FCSTD DOCUMENT  (FreeCAD 1.0R39285 (Git))
Label: optical-system
License: All rights reserved
objects: Part::Feature×51, App::Link×23, App::FeaturePython×23, App::Part×13, PartDesign::FeatureBase×1, Sketcher::SketchObject×1, PartDesign::Pocket×1, PartDesign::Body×1, Assembly::JointGroup×1, Assembly::AssemblyObject×1
note: 59 computed .brp shape members not serialized (recipe doc carries the construction recipe); baked Part::Feature solids carry a one-line shape summary decoded from their .brp

FEATURE [Part::Feature] Part__Feature  label="TTN210411-E0W"
  shape: bbox 50.8 x 39.62 x 50.8 mm, 414 faces (baked)
FEATURE [Part::Feature] Part__Feature001  label="TTN210411-E0W001"
  shape: bbox 5.001 x 4.001 x 4.001 mm, 29 faces (baked)
FEATURE [Part::Feature] Part__Feature002  label="TTN210411-E0W002"
  shape: bbox 5.001 x 4.001 x 4.001 mm, 29 faces (baked)
FEATURE [Part::Feature] Part__Feature003  label="TTN210411-E0W003"
  shape: bbox 5.001 x 4.001 x 4.001 mm, 29 faces (baked)
FEATURE [Part::Feature] Part__Feature004  label="TTN210411-E0W004"
  shape: bbox 5.001 x 4.001 x 4.001 mm, 29 faces (baked)
FEATURE [Part::Feature] Part__Feature005  label="TTN210411-E0W005"
  shape: bbox 5.001 x 4.001 x 4.001 mm, 29 faces (baked)
FEATURE [Part::Feature] Part__Feature006  label="TTN210411-E0W006"
  shape: bbox 5.001 x 4.001 x 4.001 mm, 29 faces (baked)
FEATURE [Part::Feature] Part__Feature007  label="TTN210411-E0W007"
  shape: bbox 5.001 x 4.001 x 4.001 mm, 29 faces (baked)
FEATURE [Part::Feature] Part__Feature008  label="TTN210411-E0W008"
  shape: bbox 5.001 x 4.001 x 4.001 mm, 29 faces (baked)
FEATURE [App::Part] TTN210411_E0W  label="C6WR"
  Group = -> [Part__Feature,Part__Feature001,Part__Feature002,Part__Feature003,Part__Feature004,Part__Feature005,Part__Feature006,Part__Feature007,Part__Feature008]
  Origin = -> Origin001
FEATURE [App::Link] C6WR  label="C6WR001"
  LinkPlacement = pos=(25.4,-25.4,5.02654e-06) rot=(0.577351,0.57735,-0.57735;2.0944rad)
  LinkedObject = -> TTN210411_E0W
  Placement = pos=(25.4,-25.4,5.02654e-06) rot=(0.577351,0.57735,-0.57735;2.0944rad)
FEATURE [App::FeaturePython] GroundedJoint  # Assembly grounded joint (typed FeaturePython)
  ObjectToGround = -> C6WR
  Placement = pos=(25.4,-25.4,5.02654e-06) rot=(0.577351,0.57735,-0.57735;2.0944rad)
FEATURE [Part::Feature] Part__Feature009  label="20587-E0W"
  shape: bbox 18.51 x 30.48 x 30.48 mm, 108 faces (baked)
FEATURE [Part::Feature] Part__Feature010  label="20587-E0W001"
  shape: bbox 10 x 32.78 x 32.91 mm, 10 faces (baked)
FEATURE [Part::Feature] Part__Feature011  label="20587-E0W002"
  shape: bbox 10.38 x 35.13 x 35.16 mm, 27 faces (baked)
FEATURE [Part::Feature] Part__Feature012  label="20587-E0W003"
  shape: bbox 2.484 x 26.29 x 30.36 mm, 38 faces (baked)
FEATURE [App::Part] _0587_E0W  label="AC254-040-A-ML"
  Group = -> [Part__Feature009,Part__Feature010,Part__Feature011,Part__Feature012]
  Origin = -> Origin002
FEATURE [Part::Feature] Part__Feature013  label="0875-E0W"
  shape: bbox 5.994 x 76.2 x 5.994 mm, 20 faces (baked)
FEATURE [App::Link] ER3_000  label="ER3-001"
  LinkPlacement = pos=(11.466,16.1264,-86.4141) rot=(-1,0,0;1.5708rad)
  LinkedObject = -> _875_E0W
  Placement = pos=(11.466,16.1264,-86.4141) rot=(-1,0,0;1.5708rad)
FEATURE [App::FeaturePython] Joint  label="Fixed"  # Assembly joint (typed FeaturePython)
  Activated = true
  AngleMax = 0
  AngleMin = 0
  Detach1 = false
  Detach2 = false
  Distance = 0
  Distance2 = 0
  EnableAngleMax = false
  EnableAngleMin = false
  EnableLengthMax = false
  EnableLengthMin = false
  JointType = 0 (Fixed)
  LengthMax = 0
  LengthMin = 0
  Placement1 = pos=(-1.06592,-35.6141,-1.12644) rot=(0.57735,0.57735,0.57735;4.18879rad)
  Placement2 = pos=(50.8,-14.9999,-40.4) rot=(-0.707107,0,0.707107;3.14159rad)
  Reference1 = -> Assembly [ER3_000.Part__Feature013.Edge6,ER3_000.Part__Feature013.Edge6]
  Reference2 = -> Assembly [C6WR.Part__Feature.Edge507,C6WR.Part__Feature.Edge507]
FEATURE [App::Link] ER3_001  label="ER3-002"
  LinkPlacement = pos=(41.4659,-13.8736,-86.414) rot=(-1,0,0;1.5708rad)
  LinkedObject = -> _875_E0W
  Placement = pos=(41.4659,-13.8736,-86.414) rot=(-1,0,0;1.5708rad)
FEATURE [App::Link] ER3_002  label="ER3-003"
  LinkPlacement = pos=(9.33417,-16.1264,-86.4141) rot=(0,0.707107,-0.707107;3.14159rad)
  LinkedObject = -> _875_E0W
  Placement = pos=(9.33417,-16.1264,-86.4141) rot=(0,0.707107,-0.707107;3.14159rad)
FEATURE [App::Link] ER3_003  label="ER3-004"
  LinkPlacement = pos=(39.3341,13.8736,-86.414) rot=(0,0.707107,-0.707107;3.14159rad)
  LinkedObject = -> _875_E0W
  Placement = pos=(39.3341,13.8736,-86.414) rot=(0,0.707107,-0.707107;3.14159rad)
FEATURE [App::FeaturePython] Joint001  label="Fixed001"  # Assembly joint (typed FeaturePython)
  Activated = true
  AngleMax = 0
  AngleMin = 0
  Detach1 = false
  Detach2 = false
  Distance = 0
  Distance2 = 0
  EnableAngleMax = false
  EnableAngleMin = false
  EnableLengthMax = false
  EnableLengthMin = false
  JointType = 0 (Fixed)
  LengthMax = 0
  LengthMin = 0
  Placement1 = pos=(-1.06592,-35.6141,-1.12644) rot=(0.57735,0.57735,0.57735;4.18879rad)
  Placement2 = pos=(50.8,14.9999,-40.4) rot=(0,-1,0;1.5708rad)
  Reference1 = -> Assembly [ER3_003.Part__Feature013.Edge6,ER3_003.Part__Feature013.Edge6]
  Reference2 = -> Assembly [C6WR.Part__Feature.Edge505,C6WR.Part__Feature.Edge505]
FEATURE [App::FeaturePython] Joint002  label="Fixed002"  # Assembly joint (typed FeaturePython)
  Activated = true
  AngleMax = 0
  AngleMin = 0
  Detach1 = false
  Detach2 = false
  Distance = 0
  Distance2 = 0
  EnableAngleMax = false
  EnableAngleMin = false
  EnableLengthMax = false
  EnableLengthMin = false
  JointType = 0 (Fixed)
  LengthMax = 0
  LengthMin = 0
  Placement1 = pos=(-1.06592,-35.6141,-1.12644) rot=(0.57735,0.57735,0.57735;4.18879rad)
  Placement2 = pos=(50.8,-14.9999,-10.4) rot=(0,-1,0;1.5708rad)
  Reference1 = -> Assembly [ER3_002.Part__Feature013.Edge6,ER3_002.Part__Feature013.Edge6]
  Reference2 = -> Assembly [C6WR.Part__Feature.Edge506,C6WR.Part__Feature.Edge506]
FEATURE [App::FeaturePython] Joint003  label="Fixed003"  # Assembly joint (typed FeaturePython)
  Activated = true
  AngleMax = 0
  AngleMin = 0
  Detach1 = false
  Detach2 = false
  Distance = 0
  Distance2 = 0
  EnableAngleMax = false
  EnableAngleMin = false
  EnableLengthMax = false
  EnableLengthMin = false
  JointType = 0 (Fixed)
  LengthMax = 0
  LengthMin = 0
  Placement1 = pos=(-1.06592,-35.6141,-1.12644) rot=(0.57735,0.57735,0.57735;4.18879rad)
  Placement2 = pos=(50.8,14.9999,-10.4) rot=(-0.707107,0,0.707107;3.14159rad)
  Reference1 = -> Assembly [ER3_001.Part__Feature013.Edge6,ER3_001.Part__Feature013.Edge6]
  Reference2 = -> Assembly [C6WR.Part__Feature.Edge504,C6WR.Part__Feature.Edge504]
FEATURE [Part::Feature] Part__Feature015  label="0875-E0W002"
  shape: bbox 3.285 x 6.668 x 2.845 mm, 51 faces (baked)
FEATURE [App::Part] _875_E0W  label="ER3-000"
  Group = -> [Part__Feature013,Part__Feature015]
  Origin = -> Origin003
FEATURE [Part::Feature] Part__Feature016  label="TTN189114-E0W"
  shape: bbox 40.64 x 40.64 x 8.89 mm, 368 faces (baked)
FEATURE [Part::Feature] Part__Feature017  label="TTN189114-E0W001"
  shape: bbox 5.001 x 4.001 x 4.001 mm, 29 faces (baked)
FEATURE [Part::Feature] Part__Feature018  label="TTN189114-E0W002"
  shape: bbox 5.001 x 4.001 x 4.001 mm, 29 faces (baked)
FEATURE [Part::Feature] Part__Feature019  label="TTN189114-E0W003"
  shape: bbox 5.001 x 4.001 x 4.001 mm, 29 faces (baked)
FEATURE [Part::Feature] Part__Feature020  label="TTN189114-E0W004"
  shape: bbox 5.001 x 4.001 x 4.001 mm, 29 faces (baked)
FEATURE [App::Part] TTN189114_E0W  label="CP33-000"
  Group = -> [Part__Feature016,Part__Feature017,Part__Feature018,Part__Feature019,Part__Feature020]
  Origin = -> Origin004
FEATURE [App::Link] CP33_000  label="CP33-001"
  LinkPlacement = pos=(25.4001,-2.5535e-05,-66.047) rot=(-0.707107,0.707107,0;3.14159rad)
  LinkedObject = -> TTN189114_E0W
  Placement = pos=(25.4001,-2.5535e-05,-66.047) rot=(-0.707107,0.707107,0;3.14159rad)
FEATURE [App::FeaturePython] Joint004  label="Fixed004"  # Assembly joint (typed FeaturePython)
  Activated = true
  AngleMax = 0
  AngleMin = 0
  Detach1 = false
  Detach2 = false
  Distance = 0
  Distance2 = 0
  EnableAngleMax = false
  EnableAngleMin = false
  EnableLengthMax = false
  EnableLengthMin = false
  JointType = 0 (Fixed)
  LengthMax = 0
  LengthMin = 0
  Offset2 = pos=(0,0,-56) rot=(0,0,1;0rad)
  Placement1 = pos=(15,15,4.191) rot=(0,0,1;0rad)
  Placement2 = pos=(-1.06592,-16.1761,-1.12644) rot=(0.57735,0.57735,0.57735;4.18879rad)
  Reference1 = -> Assembly [CP33_000.Part__Feature016.Edge399,CP33_000.Part__Feature016.Edge399]
  Reference2 = -> Assembly [ER3_002.Part__Feature013.Edge26,ER3_002.Part__Feature013.Edge26]
FEATURE [App::Link] AC254_040_A_ML  label="AC254-040-A-ML001"
  LinkPlacement = pos=(26.1111,6.72322,-89.4656) rot=(0.577351,0.57735,-0.57735;2.0944rad)
  LinkedObject = -> _0587_E0W
  Placement = pos=(26.1111,6.72322,-89.4656) rot=(0.577351,0.57735,-0.57735;2.0944rad)
FEATURE [App::FeaturePython] Joint005  label="Fixed005"  # Assembly joint (typed FeaturePython)
  Activated = true
  AngleMax = 0
  AngleMin = 0
  Detach1 = false
  Detach2 = false
  Distance = 0
  Distance2 = 0
  EnableAngleMax = false
  EnableAngleMin = false
  EnableLengthMax = false
  EnableLengthMin = false
  JointType = 0 (Fixed)
  LengthMax = 0
  LengthMin = 0
  Placement1 = pos=(-19.4136,-0.711014,6.72325) rot=(0,-1,0;1.5708rad)
  Placement2 = pos=(-4.16e-14,-3.12e-14,4.00506) rot=(0,0,1;0rad)
  Reference1 = -> Assembly [AC254_040_A_ML.Part__Feature009.Edge7,AC254_040_A_ML.Part__Feature009.Edge7]
  Reference2 = -> Assembly [CP33_000.Part__Feature016.Edge77,CP33_000.Part__Feature016.Edge77]
FEATURE [Part::Feature] Part__Feature021  label="TTN189038-E0W"
  shape: bbox 40.64 x 40.64 x 8.89 mm, 607 faces (baked)
FEATURE [Part::Feature] Part__Feature022  label="TTN189038-E0W001"
  shape: bbox 5.001 x 4.001 x 4.001 mm, 29 faces (baked)
FEATURE [Part::Feature] Part__Feature023  label="TTN189038-E0W002"
  shape: bbox 5.001 x 4.001 x 4.001 mm, 29 faces (baked)
FEATURE [Part::Feature] Part__Feature024  label="TTN189038-E0W003"
  shape: bbox 5.001 x 4.001 x 4.001 mm, 29 faces (baked)
FEATURE [Part::Feature] Part__Feature025  label="TTN189038-E0W004"
  shape: bbox 5.001 x 4.001 x 4.001 mm, 29 faces (baked)
FEATURE [App::Part] TTN189038_E0W  label="CP42-000"
  Group = -> [Part__Feature021,Part__Feature022,Part__Feature023,Part__Feature024,Part__Feature025]
  Origin = -> Origin005
FEATURE [App::Link] CP42_000  label="CP42-001"
  LinkPlacement = pos=(7.29353,-2.18583,-119.261) rot=(1,0,0;3.14159rad)
  LinkedObject = -> TTN189038_E0W
  Placement = pos=(7.29353,-2.18583,-119.261) rot=(1,0,0;3.14159rad)
FEATURE [App::FeaturePython] Joint006  label="Fixed006"  # Assembly joint (typed FeaturePython)
  Activated = true
  AngleMax = 0
  AngleMin = 0
  Detach1 = false
  Detach2 = false
  Distance = 0
  Distance2 = 0
  EnableAngleMax = false
  EnableAngleMin = false
  EnableLengthMax = false
  EnableLengthMin = false
  JointType = 0 (Fixed)
  LengthMax = 0
  LengthMin = 0
  Offset2 = pos=(0,0,-20) rot=(0,0,-1;1.5708rad)
  Placement1 = pos=(3.10658,12.8142,-12.2606) rot=(1,0,0;3.14159rad)
  Placement2 = pos=(-1.06592,20.5859,-1.12644) rot=(0,0.707107,0.707107;3.14159rad)
  Reference1 = -> Assembly [CP42_000.Part__Feature021.Edge53,CP42_000.Part__Feature021.Edge53]
  Reference2 = -> Assembly [ER3_002.Part__Feature013.Edge28,ER3_002.Part__Feature013.Edge28]
FEATURE [Part::Feature] Part__Feature026  label="TTN088605-E0W"
  shape: bbox 38.79 x 26.13 x 26.13 mm, 502 faces, 0 solids (baked)
FEATURE [Part::Feature] Part__Feature027  label="TTN088605-E0W001"
  shape: bbox 0.3121 x 0.2897 x 0.041 mm, 1 faces, 0 solids (baked)
FEATURE [App::Part] TTN088605_E0W  label="RMS10X"
  Group = -> [Part__Feature026,Part__Feature027]
  Origin = -> Origin006
FEATURE [App::Link] RMS10X  label="RMS10X001"
  LinkPlacement = pos=(43.629,23.975,-127.528) rot=(0,1,0;4.71239rad)
  LinkedObject = -> TTN088605_E0W
  Placement = pos=(43.629,23.975,-127.528) rot=(0,1,0;4.71239rad)
FEATURE [App::FeaturePython] Joint007  label="Fixed007"  # Assembly joint (typed FeaturePython)
  Activated = true
  AngleMax = 0
  AngleMin = 0
  Detach1 = false
  Detach2 = false
  Distance = 0
  Distance2 = 0
  EnableAngleMax = false
  EnableAngleMin = false
  EnableLengthMax = false
  EnableLengthMin = false
  JointType = 0 (Fixed)
  LengthMax = 0
  LengthMin = 0
  Offset2 = pos=(0,0,-2.5) rot=(0,0,1;0rad)
  Placement1 = pos=(14.8319,-23.975,18.2289) rot=(0,1,0;1.5708rad)
  Placement2 = pos=(18.1066,-2.18581,-6.56454) rot=(0,0,1;0rad)
  Reference1 = -> Assembly [RMS10X.Part__Feature026.Edge375,RMS10X.Part__Feature026.Edge375]
  Reference2 = -> Assembly [CP42_000.Part__Feature021.Edge25,CP42_000.Part__Feature021.Edge25]
FEATURE [Part::Feature] Part__Feature028  label="24004-E0W"
  shape: bbox 50.29 x 9.398 x 50.29 mm, 65 faces (baked)
FEATURE [Part::Feature] Part__Feature029  label="24004-E0W001"
  shape: bbox 42.67 x 12.07 x 42.67 mm, 217 faces (baked)
FEATURE [Part::Feature] Part__Feature030  label="24004-E0W002"
  shape: bbox 47.75 x 5.842 x 47.75 mm, 1692 faces (baked)
FEATURE [Part::Feature] Part__Feature031  label="24004-E0W003"
  shape: bbox 4.215 x 3.799 x 4.215 mm, 58 faces (baked)
FEATURE [App::Part] _4004_E0W  label="B3CR-000"
  Group = -> [Part__Feature028,Part__Feature029,Part__Feature030,Part__Feature031]
  Origin = -> Origin007
FEATURE [App::Link] B3CR_000  label="B3CR-001"
  LinkPlacement = pos=(48.514,-2.06884e-06,-25.4) rot=(-0.485653,0.485653,0.726831;1.88458rad)
  LinkedObject = -> _4004_E0W
  Placement = pos=(48.514,-2.06884e-06,-25.4) rot=(-0.485653,0.485653,0.726831;1.88458rad)
FEATURE [Part::Feature] Part__Feature032  label="TTN005913-E0W"
  shape: bbox 49.78 x 1.905 x 49.78 mm, 56 faces (baked)
FEATURE [Part::Feature] Part__Feature033  label="TTN005913-E0W001"
  Placement = pos=(0,0,0) rot=(0,1,0;3.92699rad)
  shape: bbox 41.91 x 8.763 x 41.91 mm, 301 faces (baked)
FEATURE [App::Part] TTN005913_E0W  label="C6WA-000"
  Group = -> [Part__Feature032,Part__Feature033]
  Origin = -> Origin008
FEATURE [App::Link] C6WA_000  label="C6WA-001"
  LinkPlacement = pos=(47.117,-1.92568e-06,-25.4) rot=(0,0,1;1.5708rad)
  LinkedObject = -> TTN005913_E0W
  Placement = pos=(47.117,-1.92568e-06,-25.4) rot=(0,0,1;1.5708rad)
FEATURE [App::FeaturePython] Joint008  label="Fixed008"  # Assembly joint (typed FeaturePython)
  Activated = true
  AngleMax = 0
  AngleMin = 0
  Detach1 = false
  Detach2 = false
  Distance = 0
  Distance2 = 0
  EnableAngleMax = false
  EnableAngleMin = false
  EnableLengthMax = false
  EnableLengthMin = false
  JointType = 0 (Fixed)
  LengthMax = 0
  LengthMin = 0
  Offset2 = pos=(0,0,0) rot=(0,0,-1;1.5708rad)
  Placement1 = pos=(19.05,1.905,19.05) rot=(0.57735,-0.57735,0.57735;2.0944rad)
  Placement2 = pos=(6.35,19.812,-44.45) rot=(0,0.707107,0.707107;3.14159rad)
  Reference1 = -> Assembly [C6WA_000.Part__Feature032.Edge63,C6WA_000.Part__Feature032.Edge63]
  Reference2 = -> Assembly [C6WR.Part__Feature.Edge523,C6WR.Part__Feature.Edge523]
FEATURE [App::FeaturePython] Joint009  label="Fixed009"  # Assembly joint (typed FeaturePython)
  Activated = true
  AngleMax = 0
  AngleMin = 0
  Detach1 = false
  Detach2 = false
  Distance = 0
  Distance2 = 0
  EnableAngleMax = false
  EnableAngleMin = false
  EnableLengthMax = false
  EnableLengthMin = false
  JointType = 0 (Fixed)
  LengthMax = 0
  LengthMin = 0
  Offset2 = pos=(0,0,0) rot=(0,0,1;0.392699rad)
  Placement1 = pos=(-1.5e-15,4.699,1.9e-15) rot=(-0.281085,0.678598,-0.678598;3.68962rad)
  Placement2 = pos=(0,3.302,0) rot=(-0.427192,-0.639338,-0.639338;2.33414rad)
  Reference1 = -> Assembly [B3CR_000.Part__Feature029.Edge36,B3CR_000.Part__Feature029.Edge36]
  Reference2 = -> Assembly [C6WA_000.Part__Feature033.Edge299,C6WA_000.Part__Feature033.Edge299]
FEATURE [Part::Feature] Part__Feature034  label="1674-E0W"
  shape: bbox 5.994 x 203.2 x 5.994 mm, 20 faces (baked)
FEATURE [Part::Feature] Part__Feature035  label="1674-E0W001"
  shape: bbox 2.927 x 6.668 x 3.281 mm, 51 faces (baked)
FEATURE [Part::Feature] Part__Feature036  label="1674-E0W002"
  shape: bbox 3.285 x 6.668 x 2.845 mm, 51 faces (baked)
FEATURE [App::Part] _674_E0W  label="ER8-000"
  Group = -> [Part__Feature034,Part__Feature035,Part__Feature036]
  Origin = -> Origin009
FEATURE [App::Link] ER8_000  label="ER8-001"
  LinkPlacement = pos=(11.466,72.9521,-9.27359) rot=(0.190732,-0.96219,-0.190732;1e-06rad)
  LinkedObject = -> _674_E0W
  Placement = pos=(11.466,72.9521,-9.27359) rot=(0.190732,-0.96219,-0.190732;1e-06rad)
FEATURE [App::Link] ER8_001  label="ER8-002"
  LinkPlacement = pos=(9.33413,72.9521,-41.5264) rot=(0,1,0;3.14159rad)
  LinkedObject = -> _674_E0W
  Placement = pos=(9.33413,72.9521,-41.5264) rot=(0,1,0;3.14159rad)
FEATURE [App::Link] ER8_002  label="ER8-003"
  LinkPlacement = pos=(41.4659,72.9521,-39.2735) rot=(0.190732,-0.96219,-0.190732;1e-06rad)
  LinkedObject = -> _674_E0W
  Placement = pos=(41.4659,72.9521,-39.2735) rot=(0.190732,-0.96219,-0.190732;1e-06rad)
FEATURE [App::Link] ER8_003  label="ER8-004"
  LinkPlacement = pos=(39.3341,72.9521,-11.5264) rot=(0,1,0;3.14159rad)
  LinkedObject = -> _674_E0W
  Placement = pos=(39.3341,72.9521,-11.5264) rot=(0,1,0;3.14159rad)
FEATURE [App::FeaturePython] Joint010  label="Fixed010"  # Assembly joint (typed FeaturePython)
  Activated = true
  AngleMax = 0
  AngleMin = 0
  Detach1 = false
  Detach2 = false
  Distance = 0
  Distance2 = 0
  EnableAngleMax = false
  EnableAngleMin = false
  EnableLengthMax = false
  EnableLengthMin = false
  JointType = 0 (Fixed)
  LengthMax = 0
  LengthMin = 0
  Placement1 = pos=(-1.06592,-98.3521,-1.12644) rot=(0.57735,0.57735,0.57735;4.18879rad)
  Placement2 = pos=(10.4,15,0) rot=(1,0,0;3.14159rad)
  Reference1 = -> Assembly [ER8_003.Part__Feature034.Edge23,ER8_003.Part__Feature034.Edge23]
  Reference2 = -> Assembly [C6WR.Part__Feature.Edge397,C6WR.Part__Feature.Edge397]
FEATURE [App::FeaturePython] Joint011  label="Fixed011"  # Assembly joint (typed FeaturePython)
  Activated = true
  AngleMax = 0
  AngleMin = 0
  Detach1 = false
  Detach2 = false
  Distance = 0
  Distance2 = 0
  EnableAngleMax = false
  EnableAngleMin = false
  EnableLengthMax = false
  EnableLengthMin = false
  JointType = 0 (Fixed)
  LengthMax = 0
  LengthMin = 0
  Placement1 = pos=(-1.06592,-98.3521,-1.12644) rot=(0.57735,0.57735,0.57735;4.18879rad)
  Placement2 = pos=(40.4,15,0) rot=(0,1,0;3.14159rad)
  Reference1 = -> Assembly [ER8_002.Part__Feature034.Edge23,ER8_002.Part__Feature034.Edge23]
  Reference2 = -> Assembly [C6WR.Part__Feature.Edge394,C6WR.Part__Feature.Edge394]
FEATURE [App::FeaturePython] Joint012  label="Fixed012"  # Assembly joint (typed FeaturePython)
  Activated = true
  AngleMax = 0
  AngleMin = 0
  Detach1 = false
  Detach2 = false
  Distance = 0
  Distance2 = 0
  EnableAngleMax = false
  EnableAngleMin = false
  EnableLengthMax = false
  EnableLengthMin = false
  JointType = 0 (Fixed)
  LengthMax = 0
  LengthMin = 0
  Placement1 = pos=(-1.06592,-98.3521,-1.12644) rot=(0.57735,0.57735,0.57735;4.18879rad)
  Placement2 = pos=(10.4,-15,0) rot=(0,1,0;3.14159rad)
  Reference1 = -> Assembly [ER8_000.Part__Feature034.Edge23,ER8_000.Part__Feature034.Edge23]
  Reference2 = -> Assembly [C6WR.Part__Feature.Edge396,C6WR.Part__Feature.Edge396]
FEATURE [App::FeaturePython] Joint013  label="Fixed013"  # Assembly joint (typed FeaturePython)
  Activated = true
  AngleMax = 0
  AngleMin = 0
  Detach1 = false
  Detach2 = false
  Distance = 0
  Distance2 = 0
  EnableAngleMax = false
  EnableAngleMin = false
  EnableLengthMax = false
  EnableLengthMin = false
  JointType = 0 (Fixed)
  LengthMax = 0
  LengthMin = 0
  Placement1 = pos=(-1.06592,-98.3521,-1.12644) rot=(0.57735,0.57735,0.57735;4.18879rad)
  Placement2 = pos=(40.4,-15,0) rot=(1,0,0;3.14159rad)
  Reference1 = -> Assembly [ER8_001.Part__Feature034.Edge23,ER8_001.Part__Feature034.Edge23]
  Reference2 = -> Assembly [C6WR.Part__Feature.Edge395,C6WR.Part__Feature.Edge395]
FEATURE [App::Link] CP33_001  label="CP33-002"
  LinkPlacement = pos=(25.4,52.591,-25.4) rot=(1,0,0;1.5708rad)
  LinkedObject = -> TTN189114_E0W
  Placement = pos=(25.4,52.591,-25.4) rot=(1,0,0;1.5708rad)
FEATURE [App::Link] AC254_040_A_ML001  label="AC254-040-A-ML002"
  LinkPlacement = pos=(32.1233,29.4944,-24.689) rot=(0.57735,-0.57735,-0.57735;2.0944rad)
  LinkedObject = -> _0587_E0W
  Placement = pos=(32.1233,29.4944,-24.689) rot=(0.57735,-0.57735,-0.57735;2.0944rad)
FEATURE [App::Link] CP33_002  label="CP33-003"
  LinkPlacement = pos=(25.4,122.481,-25.4) rot=(1,0,0;1.5708rad)
  LinkedObject = -> TTN189114_E0W
  Placement = pos=(25.4,122.481,-25.4) rot=(1,0,0;1.5708rad)
FEATURE [App::FeaturePython] Joint014  label="Fixed014"  # Assembly joint (typed FeaturePython)
  Activated = true
  AngleMax = 0
  AngleMin = 0
  Detach1 = false
  Detach2 = false
  Distance = 0
  Distance2 = 0
  EnableAngleMax = false
  EnableAngleMin = false
  EnableLengthMax = false
  EnableLengthMin = false
  JointType = 0 (Fixed)
  LengthMax = 0
  LengthMin = 0
  Offset2 = pos=(0,0,23) rot=(0,0,-1;1.5708rad)
  Placement1 = pos=(15,15,4.191) rot=(0,0,1;0rad)
  Placement2 = pos=(10.4,15,-73.8) rot=(0.707107,0.707107,0;3.14159rad)
  Reference1 = -> Assembly [CP33_001.Part__Feature016.Edge399,CP33_001.Part__Feature016.Edge399]
  Reference2 = -> Assembly [C6WR.Part__Feature.Edge489,C6WR.Part__Feature.Edge489]
FEATURE [App::FeaturePython] Joint015  label="Fixed015"  # Assembly joint (typed FeaturePython)
  Activated = true
  AngleMax = 0
  AngleMin = 0
  Detach1 = false
  Detach2 = false
  Distance = 0
  Distance2 = 0
  EnableAngleMax = false
  EnableAngleMin = false
  EnableLengthMax = false
  EnableLengthMin = false
  JointType = 0 (Fixed)
  LengthMax = 0
  LengthMin = 0
  Placement1 = pos=(-18.6516,-0.711014,6.72325) rot=(-0.707107,0,0.707107;3.14159rad)
  Placement2 = pos=(-4.16e-14,-3.12e-14,4.445) rot=(1,0,0;3.14159rad)
  Reference1 = -> Assembly [AC254_040_A_ML001.Part__Feature009.Edge20,AC254_040_A_ML001.Part__Feature009.Edge20]
  Reference2 = -> Assembly [CP33_001.Part__Feature016.Edge377,CP33_001.Part__Feature016.Edge377]
FEATURE [App::FeaturePython] Joint016  label="Fixed016"  # Assembly joint (typed FeaturePython)
  Activated = true
  AngleMax = 0
  AngleMin = 0
  Detach1 = false
  Detach2 = false
  Distance = 0
  Distance2 = 0
  EnableAngleMax = false
  EnableAngleMin = false
  EnableLengthMax = false
  EnableLengthMin = false
  JointType = 0 (Fixed)
  LengthMax = 0
  LengthMin = 0
  Offset2 = pos=(0,0,-61) rot=(0,0,1;0rad)
  Placement1 = pos=(15,15,4.445) rot=(1,0,0;3.14159rad)
  Placement2 = pos=(15,15,-65.445) rot=(0,0,1;0rad)
  Reference1 = -> Assembly [CP33_002.Part__Feature016.Edge374,CP33_002.Part__Feature016.Edge374]
  Reference2 = -> Assembly [CP33_001.Part__Feature016.Edge388,CP33_001.Part__Feature016.Edge388]
  expr: .Offset2.Base.z = -61
FEATURE [Part::Feature] Part__Feature037  label="TTN195857-E0W"
  shape: bbox 30.48 x 30.48 x 11.43 mm, 89 faces (baked)
FEATURE [Part::Feature] Part__Feature038  label="TTN195857-E0W001"
  shape: bbox 25 x 25 x 1.302 mm, 8 faces (baked)
FEATURE [Part::Feature] Part__Feature039  label="TTN195857-E0W002"
  shape: bbox 26.29 x 26.29 x 2.032 mm, 29 faces (baked)
FEATURE [App::Part] TTN195857_E0W  label="NE07A-000"
  Group = -> [Part__Feature037,Part__Feature038,Part__Feature039]
  Origin = -> Origin010
FEATURE [App::Link] NE07A_000  label="NE07A-001"
  LinkPlacement = pos=(25.4,114.809,-25.4) rot=(-0.57735,0.57735,0.57735;2.0944rad)
  LinkedObject = -> TTN195857_E0W
  Placement = pos=(25.4,114.809,-25.4) rot=(-0.57735,0.57735,0.57735;2.0944rad)
FEATURE [App::FeaturePython] Joint017  label="Fixed017"  # Assembly joint (typed FeaturePython)
  Activated = true
  AngleMax = 0
  AngleMin = 0
  Detach1 = false
  Detach2 = false
  Distance = 0
  Distance2 = 0
  EnableAngleMax = false
  EnableAngleMin = false
  EnableLengthMax = false
  EnableLengthMin = false
  JointType = 0 (Fixed)
  LengthMax = 0
  LengthMin = 0
  Offset2 = pos=(0,0,1) rot=(0,0,1;0rad)
  Placement1 = pos=(0,6e-16,2.667) rot=(0,0,-1;1.5708rad)
  Placement2 = pos=(-4.16e-14,-3.12e-14,5.00506) rot=(0,0,1;0rad)
  Reference1 = -> Assembly [NE07A_000.Part__Feature037.Edge498,NE07A_000.Part__Feature037.Edge498]
  Reference2 = -> Assembly [CP33_002.Part__Feature016.Edge393,CP33_002.Part__Feature016.Edge393]
FEATURE [App::Link] CP33_003  label="CP33-004"
  LinkPlacement = pos=(25.4,146.371,-25.4) rot=(1,0,0;1.5708rad)
  LinkedObject = -> TTN189114_E0W
  Placement = pos=(25.4,146.371,-25.4) rot=(1,0,0;1.5708rad)
FEATURE [App::FeaturePython] Joint018  label="Fixed018"  # Assembly joint (typed FeaturePython)
  Activated = true
  AngleMax = 0
  AngleMin = 0
  Detach1 = false
  Detach2 = false
  Distance = 0
  Distance2 = 0
  EnableAngleMax = false
  EnableAngleMin = false
  EnableLengthMax = false
  EnableLengthMin = false
  JointType = 0 (Fixed)
  LengthMax = 0
  LengthMin = 0
  Offset2 = pos=(0,0,-15) rot=(0,0,1;0rad)
  Placement1 = pos=(-15,15,4.445) rot=(1,0,0;3.14159rad)
  Placement2 = pos=(-15,15,-19.445) rot=(0,0,1;0rad)
  Reference1 = -> Assembly [CP33_003.Part__Feature016.Edge373,CP33_003.Part__Feature016.Edge373]
  Reference2 = -> Assembly [CP33_002.Part__Feature016.Edge387,CP33_002.Part__Feature016.Edge387]
FEATURE [Part::Feature] Part__Feature040  label="20590-E0W"
  shape: bbox 17.81 x 30.48 x 30.48 mm, 108 faces (baked)
FEATURE [Part::Feature] Part__Feature041  label="20590-E0W001"
  shape: bbox 8 x 31.01 x 31.78 mm, 10 faces (baked)
FEATURE [Part::Feature] Part__Feature042  label="20590-E0W002"
  shape: bbox 8.594 x 32.05 x 32.08 mm, 27 faces (baked)
FEATURE [Part::Feature] Part__Feature043  label="20590-E0W003"
  shape: bbox 2.484 x 26.29 x 30.36 mm, 38 faces (baked)
FEATURE [App::Part] _0590_E0W  label="AC254-060-A-ML-000"
  Group = -> [Part__Feature040,Part__Feature041,Part__Feature042,Part__Feature043]
  Origin = -> Origin011
FEATURE [App::Link] AC254_060_A_ML_000  label="AC254-060-A-ML-001"
  LinkPlacement = pos=(25.4,135.8,-25.4) rot=(-0.57735,0.57735,-0.57735;2.0944rad)
  LinkedObject = -> _0590_E0W
  Placement = pos=(25.4,135.8,-25.4) rot=(-0.57735,0.57735,-0.57735;2.0944rad)
FEATURE [App::FeaturePython] Joint019  label="Fixed019"  # Assembly joint (typed FeaturePython)
  Activated = true
  AngleMax = 0
  AngleMin = 0
  Detach1 = false
  Detach2 = false
  Distance = 0
  Distance2 = 0
  EnableAngleMax = false
  EnableAngleMin = false
  EnableLengthMax = false
  EnableLengthMin = false
  JointType = 0 (Fixed)
  LengthMax = 0
  LengthMin = 0
  Placement1 = pos=(-6.126,0,0) rot=(0,-1,0;1.5708rad)
  Placement2 = pos=(-4.16e-14,-3.12e-14,4.445) rot=(1,0,0;3.14159rad)
  Reference1 = -> Assembly [AC254_060_A_ML_000.Part__Feature040.Edge10,AC254_060_A_ML_000.Part__Feature040.Edge10]
  Reference2 = -> Assembly [CP33_003.Part__Feature016.Edge377,CP33_003.Part__Feature016.Edge377]
FEATURE [Part::Feature] Part__Feature044  label="19252-E0W"
  shape: bbox 34.16 x 7.366 x 33.66 mm, 254 faces (baked)
FEATURE [Part::Feature] Part__Feature045  label="19252-E0W001"
  shape: bbox 7.62 x 7.112 x 16.51 mm, 26 faces (baked)
FEATURE [Part::Feature] Part__Feature046  label="19252-E0W002"
  shape: bbox 7.62 x 7.112 x 16.51 mm, 26 faces (baked)
FEATURE [Part::Feature] Part__Feature047  label="19252-E0W003"
  shape: bbox 1.718 x 1.718 x 15.88 mm, 8 faces (baked)
FEATURE [Part::Feature] Part__Feature048  label="19252-E0W004"
  shape: bbox 1.718 x 1.718 x 15.88 mm, 8 faces (baked)
FEATURE [Part::Feature] Part__Feature049  label="19252-E0W005"
  shape: bbox 2.237 x 2.233 x 8.434 mm, 34 faces (baked)
FEATURE [Part::Feature] Part__Feature050  label="19252-E0W006"
  shape: bbox 2.237 x 2.234 x 8.434 mm, 34 faces (baked)
FEATURE [App::Part] _9252_E0W  label="FFM-1-000"
  Group = -> [Part__Feature044,Part__Feature045,Part__Feature046,Part__Feature047,Part__Feature048,Part__Feature049,Part__Feature050]
  Origin = -> Origin012
FEATURE [App::Link] FFM_1_000  label="FFM-1-001"
  LinkPlacement = pos=(35.052,-0.0180319,-25.382) rot=(0.678598,-0.678598,-0.281085;3.68962rad)
  LinkedObject = -> _9252_E0W
  Placement = pos=(35.052,-0.0180319,-25.382) rot=(0.678598,-0.678598,-0.281085;3.68962rad)
FEATURE [App::FeaturePython] Joint020  label="Fixed020"  # Assembly joint (typed FeaturePython)
  Activated = true
  AngleMax = 0
  AngleMin = 0
  Detach1 = false
  Detach2 = false
  Distance = 0
  Distance2 = 0
  EnableAngleMax = false
  EnableAngleMin = false
  EnableLengthMax = false
  EnableLengthMin = false
  JointType = 0 (Fixed)
  LengthMax = 0
  LengthMin = 0
  Offset1 = pos=(-0.8,0,0) rot=(0,0,1;0rad)
  Offset2 = pos=(0,0,0) rot=(0,0,1;0.785398rad)
  Placement1 = pos=(0,0,-13.5) rot=(0.57735,0.57735,0.57735;4.18879rad)
  Placement2 = pos=(13.5255,12.065,3.55e-14) rot=(0,-0.707107,0.707107;3.14159rad)
  Reference1 = -> Assembly [FFM_1_000.Part__Feature044.Edge38,FFM_1_000.Part__Feature044.Edge38]
  Reference2 = -> Assembly [C6WA_000.Part__Feature033.Edge206,C6WA_000.Part__Feature033.Edge206]
FEATURE [Part::Feature] Part__Feature051  label="BST10R"
  Placement = pos=(0,0,33) rot=(0,0,1;0rad)
  shape: bbox 36 x 25 x 1 mm, 36 faces (baked)
FEATURE [PartDesign::FeatureBase] BaseFeature
  BaseFeature = -> Part__Feature051
  Suppressed = false
FEATURE [Sketcher::SketchObject] Sketch
  ArcFitTolerance = 1e-06
  AttachmentSupport = -> [BaseFeature]
  FullyConstrained = true
  MakeInternals = false
  MapMode = 5
  Placement = pos=(0,-12.5,0) rot=(1,0,0;1.5708rad)
  sketch-geometry (5):
    g0: LineSegment StartX=-18 StartY=-0.75 StartZ=0 EndX=18 EndY=-0.75 EndZ=0
    g1: LineSegment StartX=18 StartY=-0.75 StartZ=0 EndX=18 EndY=0.75 EndZ=0
    g2: LineSegment StartX=18 StartY=0.75 StartZ=0 EndX=-18 EndY=0.75 EndZ=0
    g3: LineSegment StartX=-18 StartY=0.75 StartZ=0 EndX=-18 EndY=-0.75 EndZ=0
    g4: GeomPoint [constr] X=0 Y=0 Z=0
  constraints (12):
    c: Coincident(g0,g1)
    c: Coincident(g1,g2)
    c: Coincident(g2,g3)
    c: Coincident(g3,g0)
    c: Horizontal(g0)
    c: Horizontal(g2)
    c: Vertical(g1)
    c: Vertical(g3)
    c: Symmetric(g2,g0,g4)
    c: Distance(g1,g3) = 36
    c: Distance(g0,g2) = 1.5
    c: Coincident(g4,g-1)
FEATURE [PartDesign::Pocket] Pocket
  BaseFeature = -> BaseFeature
  Direction = (0,1,-2e-16)
  Length = 8
  Length2 = 5
  Profile = -> Sketch
  ReferenceAxis = -> Sketch [N_Axis]
  Refine = true
  Suppressed = false
  Type = 0
FEATURE [PartDesign::Body] Body
  AllowCompound = false
  BaseFeature = -> Part__Feature051
  Group = -> [BaseFeature,Sketch,Pocket]
  Origin = -> Origin014
  Tip = -> Pocket
FEATURE [App::Part] Part  label="BST10R001"
  Group = -> [Part__Feature051,Body]
  Origin = -> Origin013
FEATURE [App::Link] BST10R001  label="BST10R002"
  LinkPlacement = pos=(26.1705,1.4446,-27.8041) rot=(0.357407,-0.357407,0.862856;1.71777rad)
  LinkedObject = -> Part
  Placement = pos=(26.1705,1.4446,-27.8041) rot=(0.357407,-0.357407,0.862856;1.71777rad)
FEATURE [App::FeaturePython] Joint021  label="Fixed021"  # Assembly joint (typed FeaturePython)
  Activated = true
  AngleMax = 0
  AngleMin = 0
  Detach1 = false
  Detach2 = false
  Distance = 0
  Distance2 = 0
  EnableAngleMax = false
  EnableAngleMin = false
  EnableLengthMax = false
  EnableLengthMin = false
  JointType = 0 (Fixed)
  LengthMax = 0
  LengthMin = 0
  Offset2 = pos=(0,0,0) rot=(0,0,1;3.14159rad)
  Placement1 = pos=(-17.8,-4.5,-0.5) rot=(0.57735,0.57735,0.57735;4.18879rad)
  Placement2 = pos=(18.4785,4.3815,3.24697) rot=(0.57735,-0.57735,-0.57735;4.18879rad)
  Reference1 = -> Assembly [BST10R001.Body.Edge22,BST10R001.Body.Vertex9]
  Reference2 = -> Assembly [FFM_1_000.Part__Feature046.Edge49,FFM_1_000.Part__Feature046.Edge49]
FEATURE [Assembly::JointGroup] Joints
  Group = -> [GroundedJoint,Joint,Joint001,Joint002,Joint003,Joint004,Joint005,Joint006,Joint007,Joint008,Joint009,Joint010,Joint011,Joint012,Joint013,Joint014,Joint015,Joint016,Joint017,Joint018,Joint019,Joint020,Joint021]
FEATURE [Assembly::AssemblyObject] Assembly  label="optical-system-assembly"
  Group = -> [Joints,C6WR,GroundedJoint,ER3_000,Joint,ER3_001,ER3_002,ER3_003,Joint001,Joint002,Joint003,CP33_000,Joint004,AC254_040_A_ML,Joint005,CP42_000,Joint006,RMS10X,Joint007,B3CR_000,C6WA_000,Joint008,Joint009,ER8_000,ER8_001,ER8_002,ER8_003,Joint010,Joint011,Joint012,Joint013,CP33_001,AC254_040_A_ML001,CP33_002,Joint014,Joint015,Joint016,NE07A_000,Joint017,CP33_003,Joint018,AC254_060_A_ML_000,Joint019,+4 more]
  Origin = -> Origin
  Type = Assembly
